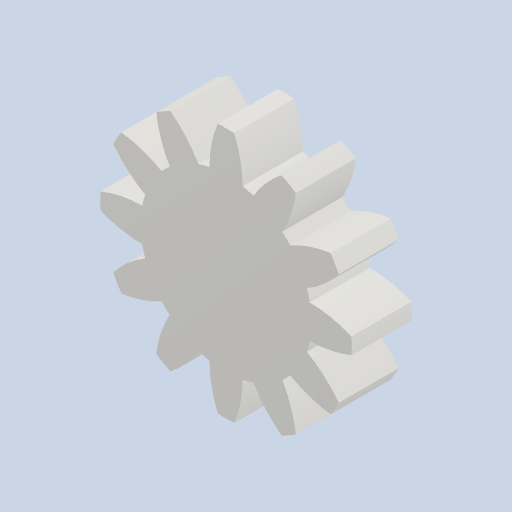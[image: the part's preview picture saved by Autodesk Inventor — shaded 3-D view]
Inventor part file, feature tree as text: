
AUTODESK INVENTOR PART (.ipt)
format: ipt  version: 2022 (Build 260153000, 153)  size: 189,952 bytes
history: native  units: mm (DEFAULTED — no unit token found)
features: plane x3, other x3, sketch x2, extrude x1
ambient origin geometry x8: Origin, YZ Plane, XZ Plane, XY Plane, X Axis, Y Axis, Z Axis, Center Point
bodies: Solid1 (feature_tree)
feature tree (9):
  extrude  "Extrusion1"  Depth=5.0mm TaperAngle=0.0deg
  plane  "Work Plane2"
  plane  "Work Plane8"
  plane  "Work Plane9"
  other  "Цилиндрическое зубчатое зацепление"
  sketch  "Sketch1"  dims[d0=20.969785mm d1=5.0mm d2=0.0mm]
  sketch  "Sketch2"  dims[d3=18.0mm d4=10.0mm d5=0.0mm d16=43.170602mm d17=0.0mm d34=15.0deg d39=0.0mm d41=0.0mm d43=43.170602mm d46=43.170602mm d47=0.0mm d48=0.0mm]
  other  "Srf1"
  other  "Средний диаметр"
